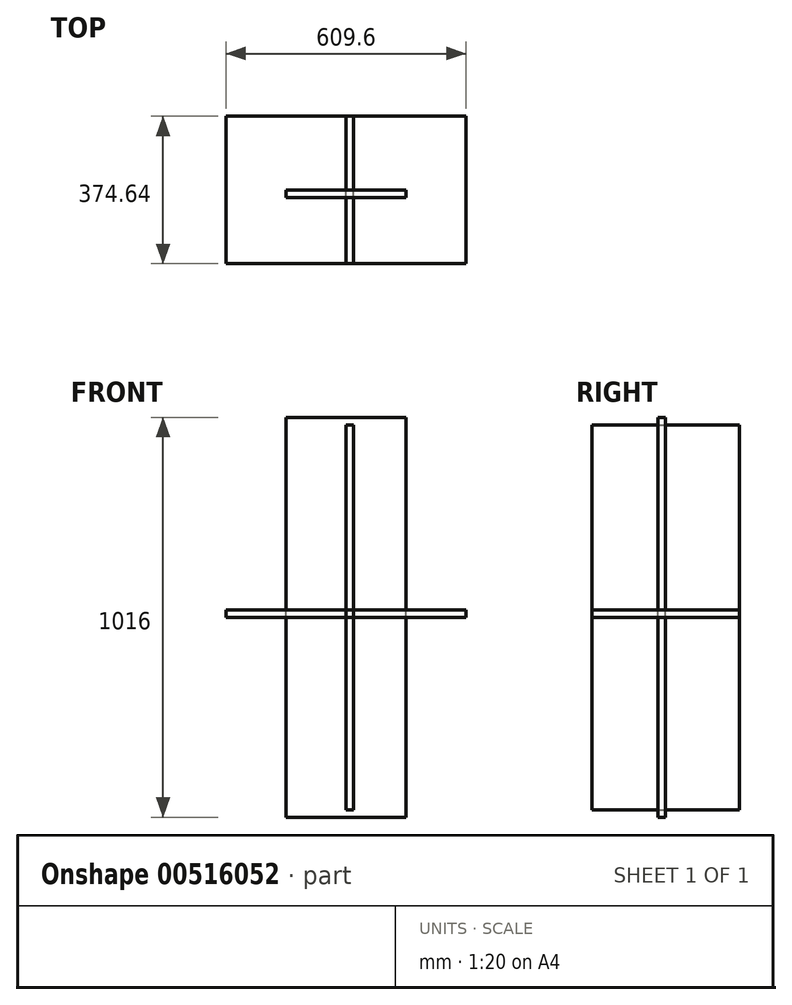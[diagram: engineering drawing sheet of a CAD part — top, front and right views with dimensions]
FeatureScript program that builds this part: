
annotation { "Feature Type Name" : "Feature", "Feature Type Description" : "" }
export const myFeature = defineFeature(function(context is Context, id is Id, definition is map)
    precondition{}
    {
        {
            var Q0;
            Q0=qCreatedBy(makeId("Top.planeOp"),FACE);
            var sketch = newSketch(context, id + "F0", { "sketchPlane" : qUnion([Q0])});
            skLineSegment(sketch, "E0.bottom", {"start": v(304.8, -187.32) * mm, "end": v(-304.8, -187.33) * mm});
            skLineSegment(sketch, "E0.top", {"start": v(304.8, 187.33) * mm, "end": v(-304.8, 187.32) * mm});
            skLineSegment(sketch, "E0.left", {"start": v(304.8, -187.32) * mm, "end": v(304.8, 187.33) * mm});
            skLineSegment(sketch, "E0.right", {"start": v(-304.8, -187.33) * mm, "end": v(-304.8, 187.32) * mm});
            skPoint(sketch, "E0.middle", {"position": v(0, 0) * mm});
            skSolve(sketch);
        }
        {
            var Q0;
            Q0=makeQuery(id+"F0.imprint","IMPRINT",FACE,{"disambiguationData":[TD([[makeQuery(id+"F0.imprint","IMPRINT",EDGE,{"derivedFrom":sQuery(id+"F0.wireOp",EDGE,"E0.bottom")}),-1.0]])]});
            extrude(context, id + "F1", {"entities" : qUnion([Q0]), "depth" : 19.05 * mm, "offsetDistance" : 25.4 * mm});
        }
        {
            var Q0;
            Q0=qCreatedBy(makeId("Right.planeOp"),FACE);
            var sketch = newSketch(context, id + "F2", { "sketchPlane" : qUnion([Q0])});
            skLineSegment(sketch, "E1.bottom", {"start": v(-187.33, -488.95) * mm, "end": v(187.33, -488.95) * mm});
            skLineSegment(sketch, "E1.top", {"start": v(-187.32, 488.95) * mm, "end": v(187.33, 488.95) * mm});
            skLineSegment(sketch, "E1.left", {"start": v(-187.33, -488.95) * mm, "end": v(-187.32, 488.95) * mm});
            skLineSegment(sketch, "E1.right", {"start": v(187.33, -488.95) * mm, "end": v(187.33, 488.95) * mm});
            skPoint(sketch, "E1.middle", {"position": v(0, 0) * mm});
            skSolve(sketch);
        }
        {
            var Q0;
            Q0=makeQuery(id+"F2.imprint","IMPRINT",FACE,{"disambiguationData":[TD([[makeQuery(id+"F2.imprint","IMPRINT",EDGE,{"derivedFrom":sQuery(id+"F2.wireOp",EDGE,"E1.bottom")}),1.0]])]});
            extrude(context, id + "F3", {"entities" : qUnion([Q0]), "depth" : 19.05 * mm, "offsetDistance" : 25.4 * mm});
        }
        {
            var Q0;
            Q0=qCreatedBy(makeId("Front.planeOp"),FACE);
            var sketch = newSketch(context, id + "F4", { "sketchPlane" : qUnion([Q0])});
            skLineSegment(sketch, "E2.bottom", {"start": v(-152.4, -508) * mm, "end": v(152.4, -508) * mm});
            skLineSegment(sketch, "E2.top", {"start": v(-152.4, 508) * mm, "end": v(152.4, 508) * mm});
            skLineSegment(sketch, "E2.left", {"start": v(-152.4, -508) * mm, "end": v(-152.4, 508) * mm});
            skLineSegment(sketch, "E2.right", {"start": v(152.4, -508) * mm, "end": v(152.4, 508) * mm});
            skPoint(sketch, "E2.middle", {"position": v(0, 0) * mm});
            skSolve(sketch);
        }
        {
            var Q0;
            Q0=makeQuery(id+"F4.imprint","IMPRINT",FACE,{"disambiguationData":[TD([[makeQuery(id+"F4.imprint","IMPRINT",EDGE,{"derivedFrom":sQuery(id+"F4.wireOp",EDGE,"E2.bottom")}),1.0]])]});
            extrude(context, id + "F5", {"entities" : qUnion([Q0]), "depth" : 19.05 * mm, "offsetDistance" : 25.4 * mm});
        }
    });
